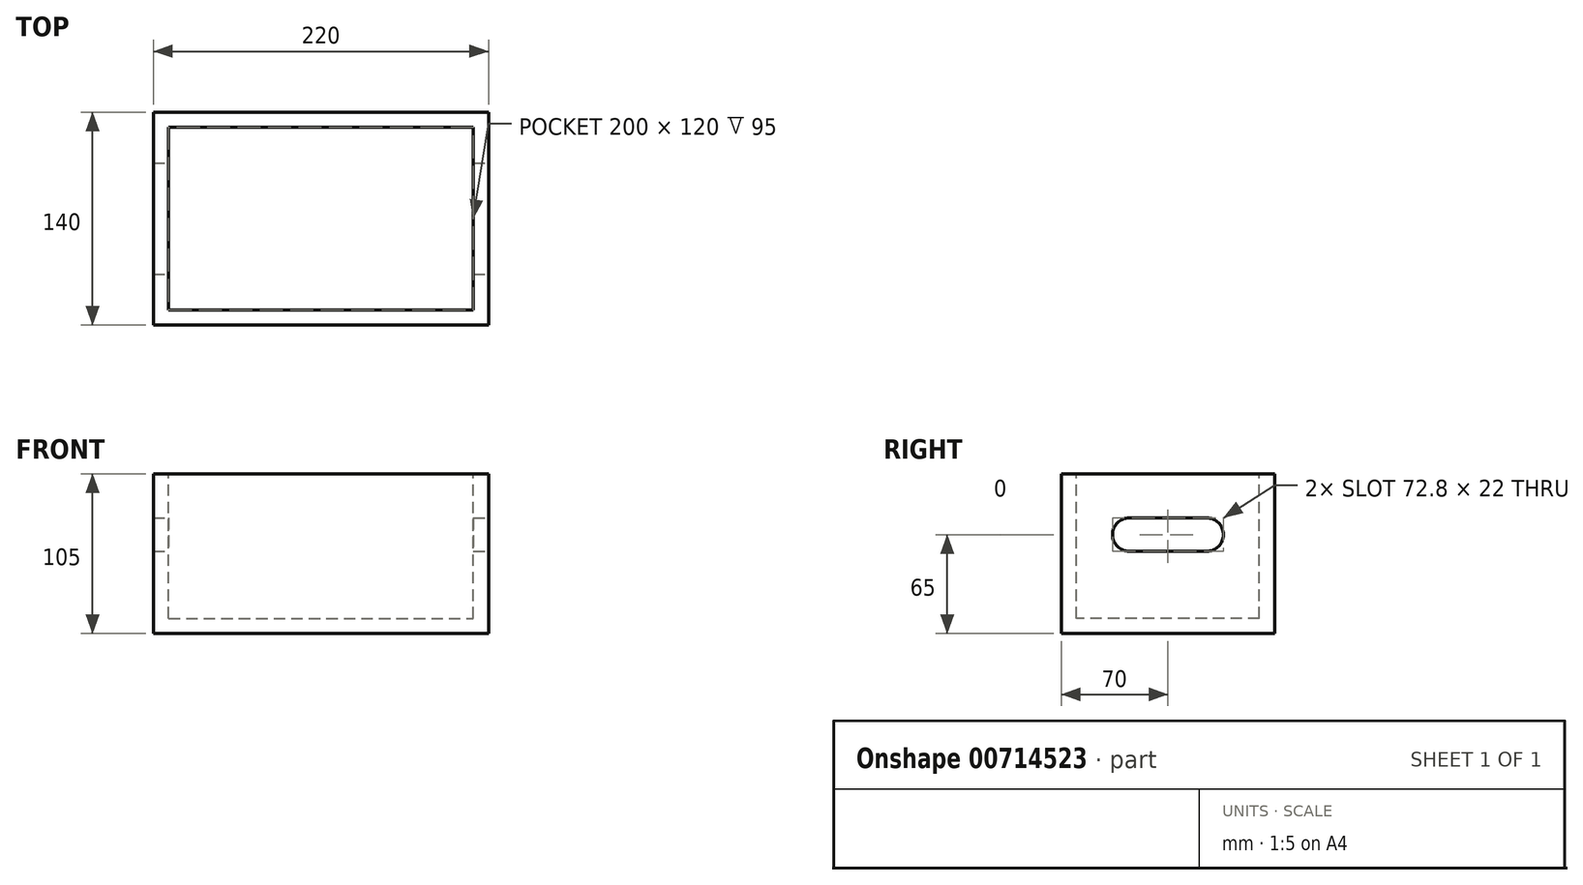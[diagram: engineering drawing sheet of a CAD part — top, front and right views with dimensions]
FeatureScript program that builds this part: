
annotation { "Feature Type Name" : "Feature", "Feature Type Description" : "" }
export const myFeature = defineFeature(function(context is Context, id is Id, definition is map)
    precondition{}
    {
        {
            var Q0;
            Q0=qCreatedBy(makeId("Front.planeOp"),FACE);
            var sketch = newSketch(context, id + "F0", { "sketchPlane" : qUnion([Q0])});
            skLineSegment(sketch, "E0.bottom", {"start": v(0, 0) * mm, "end": v(220, 0) * mm});
            skLineSegment(sketch, "E0.top", {"start": v(0, 105) * mm, "end": v(220, 105) * mm});
            skLineSegment(sketch, "E0.left", {"start": v(0, 0) * mm, "end": v(0, 105) * mm});
            skLineSegment(sketch, "E0.right", {"start": v(220, 0) * mm, "end": v(220, 105) * mm});
            skSolve(sketch);
        }
        {
            var Q0;
            Q0=makeQuery(id+"F0.imprint","IMPRINT",FACE,{"disambiguationData":[TD([[makeQuery(id+"F0.imprint","IMPRINT",EDGE,{"derivedFrom":sQuery(id+"F0.wireOp",EDGE,"E0.bottom")}),1.0]])]});
            extrude(context, id + "F1", {"entities" : qUnion([Q0]), "oppositeDirection" : true, "depth" : 140 * mm, "offsetDistance" : 25 * mm});
        }
        {
            var Q0;
            Q0=makeQuery(id+"F1.opExtrude","SWEPT_FACE",FACE,{"disambiguationData":[OSD([sQuery(id+"F0.wireOp",EDGE,"E0.top")])]});
            var sketch = newSketch(context, id + "F2", { "sketchPlane" : qUnion([Q0])});
            skLineSegment(sketch, "E1.0", {"start": v(10, 130) * mm, "end": v(210, 130) * mm});
            skLineSegment(sketch, "E2.0", {"start": v(10, 130) * mm, "end": v(10, 10) * mm});
            skLineSegment(sketch, "E3.0", {"start": v(10, 10) * mm, "end": v(210, 10) * mm});
            skLineSegment(sketch, "E4.0", {"start": v(210, 130) * mm, "end": v(210, 10) * mm});
            skSolve(sketch);
        }
        {
            var Q0;
            Q0 = qSketchRegion(id + "F2", true);
            extrude(context, id + "F3", {"entities" : qUnion([Q0]), "operationType" : NewBodyOperationType.REMOVE, "oppositeDirection" : true, "depth" : 95 * mm, "offsetDistance" : 25 * mm});
        }
        {
            var Q0;
            Q0=makeQuery(id+"F1.opExtrude","SWEPT_FACE",FACE,{"disambiguationData":[OSD([sQuery(id+"F0.wireOp",EDGE,"E0.right")])]});
            var sketch = newSketch(context, id + "F4", { "sketchPlane" : qUnion([Q0])});
            skArc(sketch, "E5", {"start": v(44.6, 76) * mm, "mid": v(33.6, 65) * mm, "end": v(44.6, 54) * mm});
            skArc(sketch, "E6", {"start": v(95.4, 54) * mm, "mid": v(106.4, 65) * mm, "end": v(95.4, 76) * mm});
            skPoint(sketch, "E7", {"position": v(70, 75) * mm});
            skLineSegment(sketch, "E8", {"start": v(44.6, 76) * mm, "end": v(95.4, 76) * mm});
            skLineSegment(sketch, "E9", {"start": v(95.4, 54) * mm, "end": v(44.6, 54) * mm});
            skSolve(sketch);
        }
        {
            var Q0;
            Q0=makeQuery(id+"F4.imprint","IMPRINT",FACE,{"disambiguationData":[TD([[makeQuery(id+"F4.imprint","IMPRINT",EDGE,{"derivedFrom":sQuery(id+"F4.wireOp",EDGE,"E5")}),1.0]])]});
            extrude(context, id + "F5", {"entities" : qUnion([Q0]), "operationType" : NewBodyOperationType.REMOVE, "endBound" : BoundingType.THROUGH_ALL, "oppositeDirection" : true, "depth" : 25 * mm, "offsetDistance" : 25 * mm});
        }
    });
